# Revit family: Panel_Leviton_Indoor_42Pos
name_source: partatom
category: Electrical Equipment
units: mm (PartAtom-declared; Revit-internal decimal feet)

## family parameters
Always vertical = No
Classification Number = 23.80.30.11.17
Cut with Voids When Loaded = No
Maintain Annotation Orientation = No
Panel Configuration = Two Columns, Circuits Across
Part Type = Panelboard
Room Calculation Point = No
Round Connector Dimension = Use Diameter
Shared = No
Work Plane-Based = Yes

## types (6) — shared parameters
Body = Galvanized Steel_White Powder Coat
Default Elevation = 48 "
Face Overlap = 0.98 "
Neutral Rating = 100.00%
Overall Height = 45.33 "
Overall Width = 16.25 "
Voltage Comments = 208
Voltage_MEP = 208 V
zero-valued in all types: Unit Depth, Unit Height, Unit Width

## per-type parameters (varying)
| type | Description | Mains Type | Model |
| LP420-MB - 240V / 200A | Indoor Load Center; NEMA 1; with Main Circuit Breaker; 200A; 42 Spaces; 22 KA interrupt rating; Enclosure and Interior only | Main Breaker | LP420-MB |
| LP422-MB - 240V / 225A | Indoor Load Center; NEMA 1; with Main Circuit Breaker; 225A; 42 Spaces; 22 KA interrupt rating; Enclosure and Interior only | Main Breaker | LP422-MB |
| LP422-ML - 240V / 225A | Indoor Load Center; NEMA 1; with Main Lugs; 225A; 42 Spaces; 22 KA interrupt rating; Enclosure and Interior only | Main Lug | LP422-ML |
| LP420-MB - 120V / 200A | Indoor Load Center; NEMA 1; with Main Circuit Breaker; 200A; 42 Spaces; 22 KA interrupt rating; Enclosure and Interior only | Main Breaker | LP420-MB |
| LP422-MB - 120V / 225A | Indoor Load Center; NEMA 1; with Main Circuit Breaker; 225A; 42 Spaces; 22 KA interrupt rating; Enclosure and Interior only | Main Breaker | LP422-MB |
| LP422-ML - 120V / 225A | Indoor Load Center; NEMA 1; with Main Lugs; 225A; 42 Spaces; 22 KA interrupt rating; Enclosure and Interior only | Main Lug | LP422-ML |

## geometry (parser evidence)
native form markers: Sweep x8
no freeform markers — native parametric forms only
